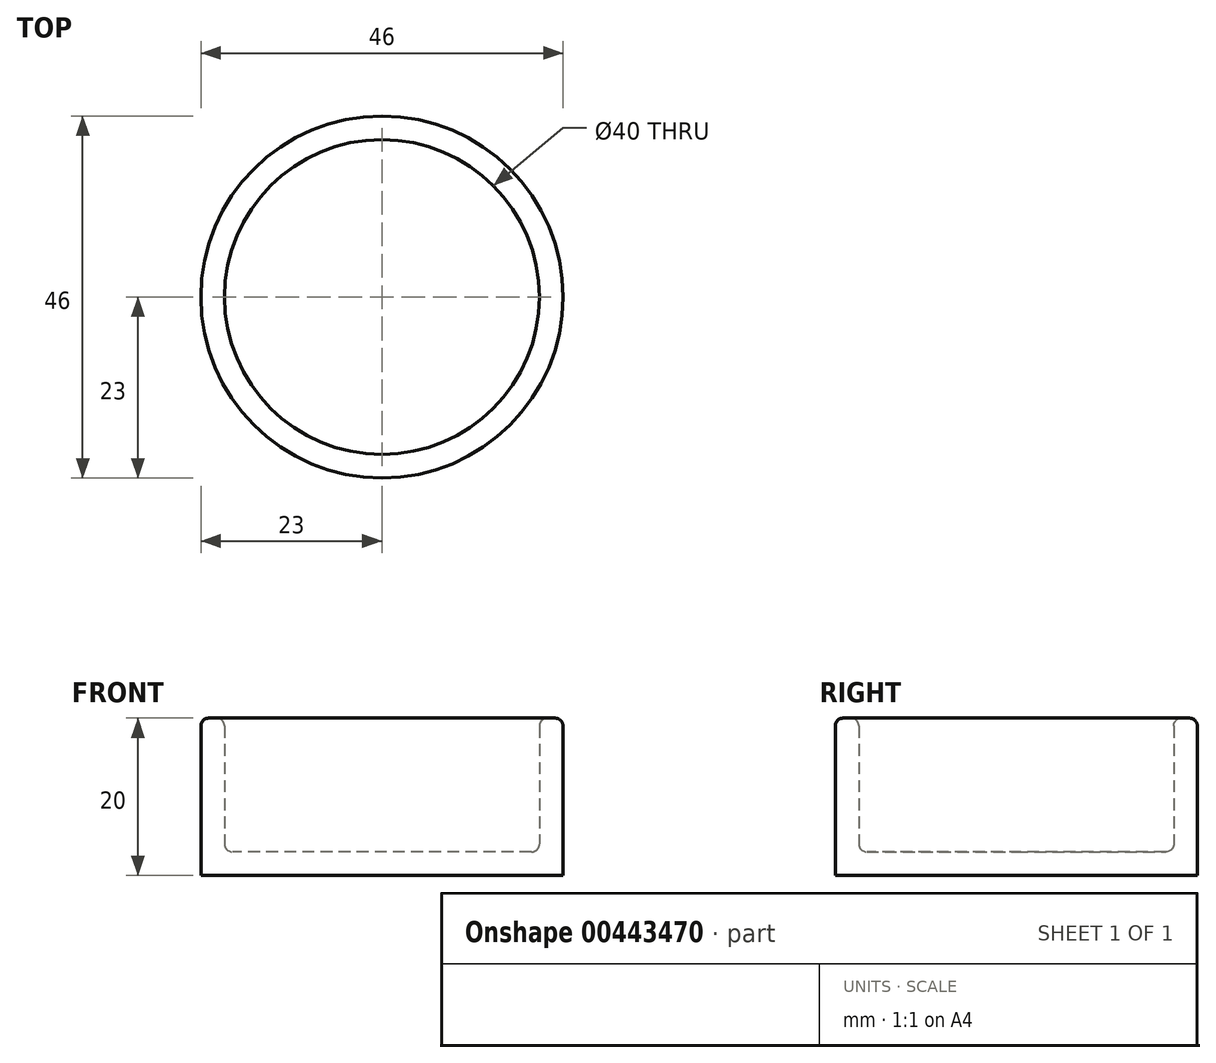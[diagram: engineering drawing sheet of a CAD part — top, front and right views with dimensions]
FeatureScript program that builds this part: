
annotation { "Feature Type Name" : "Feature", "Feature Type Description" : "" }
export const myFeature = defineFeature(function(context is Context, id is Id, definition is map)
    precondition{}
    {
        {
            var Q0;
            Q0=qCreatedBy(makeId("Top.planeOp"),FACE);
            var sketch = newSketch(context, id + "F0", { "sketchPlane" : qUnion([Q0])});
            skCircle(sketch, "E0", {"center": v(0, 0) * mm, "radius": 23 * mm});
            skCircle(sketch, "E1", {"center": v(0, 0) * mm, "radius": 20 * mm});
            skSolve(sketch);
        }
        {
            var Q0;
            Q0 = qSketchRegion(id + "F0", true);
            extrude(context, id + "F1", {"entities" : qUnion([Q0]), "depth" : 20 * mm});
        }
        {
            var Q0;
            Q0=qCreatedBy(makeId("Top.planeOp"),FACE);
            var sketch = newSketch(context, id + "F2", { "sketchPlane" : qUnion([Q0])});
            skCircle(sketch, "E2", {"center": v(0, 0) * mm, "radius": 23 * mm});
            skSolve(sketch);
        }
        {
            var Q0;
            Q0 = qSketchRegion(id + "F2", true);
            extrude(context, id + "F3", {"entities" : qUnion([Q0]), "operationType" : NewBodyOperationType.ADD, "depth" : 3 * mm});
        }
        {
            var Q0;
            Q0=makeQuery(id+"F1.opExtrude","CAP_EDGE",EDGE,{"disambiguationData":[OSD([sQuery(id+"F0.wireOp",EDGE,"E1")])],"isStart":false});
            fillet(context, id + "F4", {"entities" : qUnion([Q0]), "radius" : 1 * mm, "tangentPropagation" : true, "allowEdgeOverflow" : false});
        }
        {
            var Q0;
            Q0=makeQuery(id+"F1.opExtrude","CAP_EDGE",EDGE,{"disambiguationData":[OSD([sQuery(id+"F0.wireOp",EDGE,"E0")])],"isStart":false});
            fillet(context, id + "F5", {"entities" : qUnion([Q0]), "radius" : 1 * mm, "tangentPropagation" : true, "allowEdgeOverflow" : false});
        }
        {
            var Q0;
            Q0=makeQuery(id+"F3.boolean.opBoolean","INTERSECT",EDGE,{"derivedFrom":[makeQuery(id+"F1.opExtrude","SWEPT_FACE",FACE,{"disambiguationData":[OSD([sQuery(id+"F0.wireOp",EDGE,"E1")])]}),makeQuery(id+"F3.opExtrude","CAP_FACE",FACE,{"disambiguationData":[OSD([sQuery(id+"F2.wireOp",EDGE,"E2")])],"isStart":false})]});
            fillet(context, id + "F6", {"entities" : qUnion([Q0]), "radius" : 1 * mm, "tangentPropagation" : true, "allowEdgeOverflow" : false});
        }
    });
